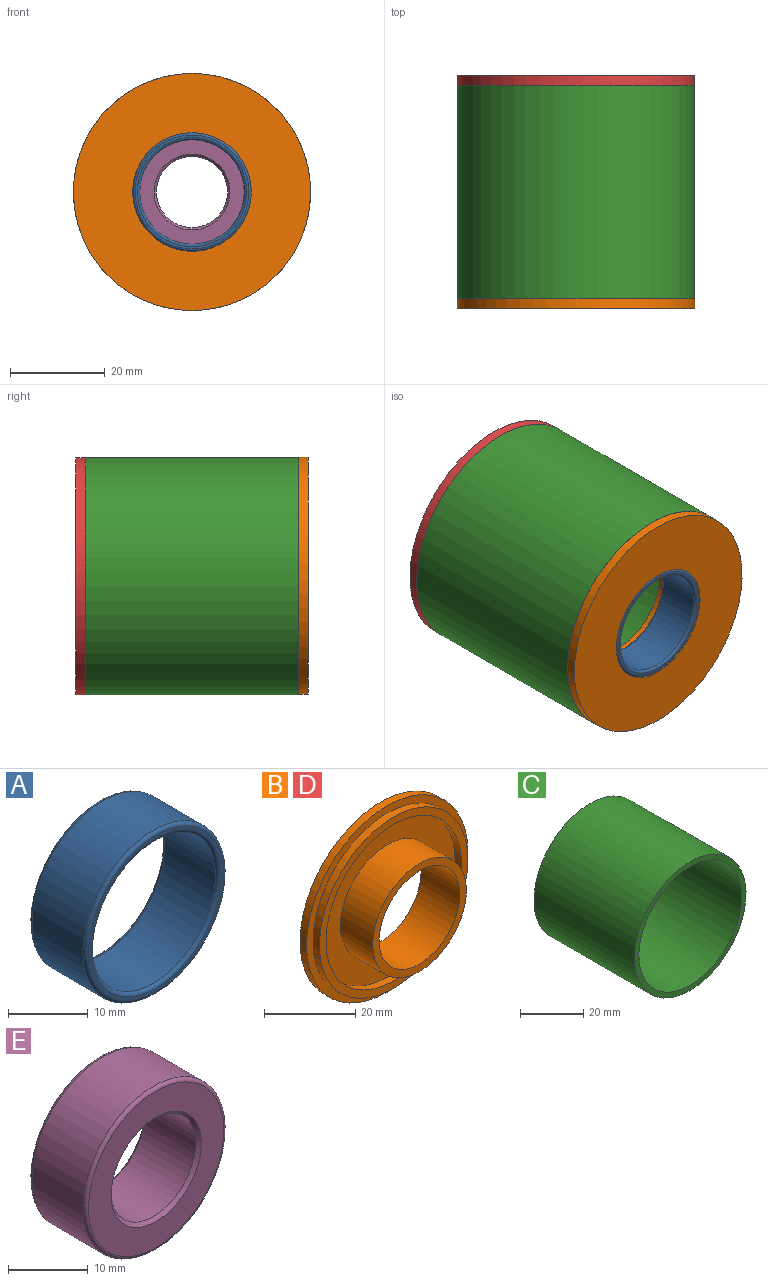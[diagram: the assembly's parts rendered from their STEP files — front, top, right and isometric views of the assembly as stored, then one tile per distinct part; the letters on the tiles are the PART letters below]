
ASSEMBLY  parts=5 mates=8
PART A: 8 faces, bbox 27.1x10x27.1 mm
  f0: cylinder r=11mm len=22mm, axis (0,1,0), area 622mm2, adj f4,f6
  f1: cylinder r=12.5mm len=25mm, axis (0,1,0), area 706.9mm2, adj f5,f7
  f2: plane 24x24mm, normal (0,-1,0), area 36.9mm2, adj f6,f7
  f3: plane 24x24mm, normal (0,1,0), area 36.9mm2, adj f4,f5
  f4: torus R=11.5mm, axis (0,-1,0), area 55.2mm2, adj f0,f3
  f5: torus R=12mm, axis (0,-1,0), area 60.8mm2, adj f1,f3
  f6: torus R=11.5mm, axis (0,-1,0), area 55.2mm2, adj f0,f2
  f7: torus R=12mm, axis (0,-1,0), area 60.8mm2, adj f1,f2
PART B: 10 faces, bbox 50x12x50 mm
  f0: cylinder r=25mm len=50mm, axis (0,1,0), area 314.2mm2, adj f1,f2
  f1: plane 50x50mm, normal (0,-1,0), area 301.6mm2, adj f0,f4
  f2: plane 50x50mm, normal (0,1,0), area 1472.6mm2, adj f0,f7
  f3: cylinder r=21mm len=42mm, axis (0,1,0), area 263.9mm2, adj f5,f6
  f4: cylinder r=23mm len=46mm, axis (0,1,0), area 289mm2, adj f1,f5
  f5: plane 46x46mm, normal (0,-1,0), area 276.5mm2, adj f3,f4
  f6: plane 42x42mm, normal (0,-1,0), area 724.9mm2, adj f3,f8
  f7: cylinder r=12.5mm len=25mm, axis (0,1,0), area 942.5mm2, adj f2,f9
  f8: cylinder r=14.5mm len=29mm, axis (0,1,0), area 911.1mm2, adj f6,f9
  f9: plane 29x29mm, normal (0,-1,0), area 169.6mm2, adj f7,f8
PART C: 4 faces, bbox 50x45x50 mm
  f0: cylinder r=23mm len=46mm, axis (0,1,0), area 6503.1mm2, adj f2,f3
  f1: cylinder r=25mm len=50mm, axis (0,1,0), area 7068.6mm2, adj f2,f3
  f2: plane 50x50mm, normal (0,-1,0), area 301.6mm2, adj f0,f1
  f3: plane 50x50mm, normal (0,1,0), area 301.6mm2, adj f0,f1
PART D: same geometry as B
PART E: 8 faces, bbox 27.1x10x27.1 mm
  f0: cylinder r=7.5mm len=15mm, axis (0,1,0), area 424.1mm2, adj f6,f7
  f1: cylinder r=12.5mm len=25mm, axis (0,1,0), area 706.9mm2, adj f4,f5
  f2: plane 24x24mm, normal (0,-1,0), area 251.3mm2, adj f5,f7
  f3: plane 24x24mm, normal (0,1,0), area 251.3mm2, adj f4,f6
  f4: torus R=12mm, axis (0,-1,0), area 60.8mm2, adj f1,f3
  f5: torus R=12mm, axis (0,-1,0), area 60.8mm2, adj f1,f2
  f6: cone r=8mm half-angle=45deg, axis (0,1,0), area 34.4mm2, adj f0,f3
  f7: cone r=7.5mm half-angle=45deg, axis (0,-1,0), area 34.4mm2, adj f0,f2
PLACE A t=(0,-19.5,0)mm
PLACE B rot(axis=(1,0,0),180deg) t=(0,-29.5,0)mm
PLACE C t=(0,17.5,0)mm
PLACE D t=(0,19.5,0)mm
PLACE E t=(0,19.5,0)mm
MATE cylindrical C.f1 <-> D.f0  axis (0,1,0) through (0,17.5,0)mm
MATE planar B.f0 <-> A.f1  axis (0,-1,0) through (0,-29.5,0)mm
MATE planar C.f0 <-> D.f3  axis (0,1,0) through (0,17.5,0)mm
MATE cylindrical B.f3 <-> A.f1  axis (0,1,0) through (0,-17.5,0)mm
MATE planar C.f1 <-> B.f3  axis (0,-1,0) through (0,-27.5,0)mm
MATE planar D.f3 <-> E.f0  axis (0,1,0) through (0,19.5,0)mm
MATE cylindrical C.f1 <-> B.f0  axis (0,1,0) through (0,-5,0)mm
MATE cylindrical C.f1 <-> E.f1  axis (0,1,0) through (0,-5,0)mm
